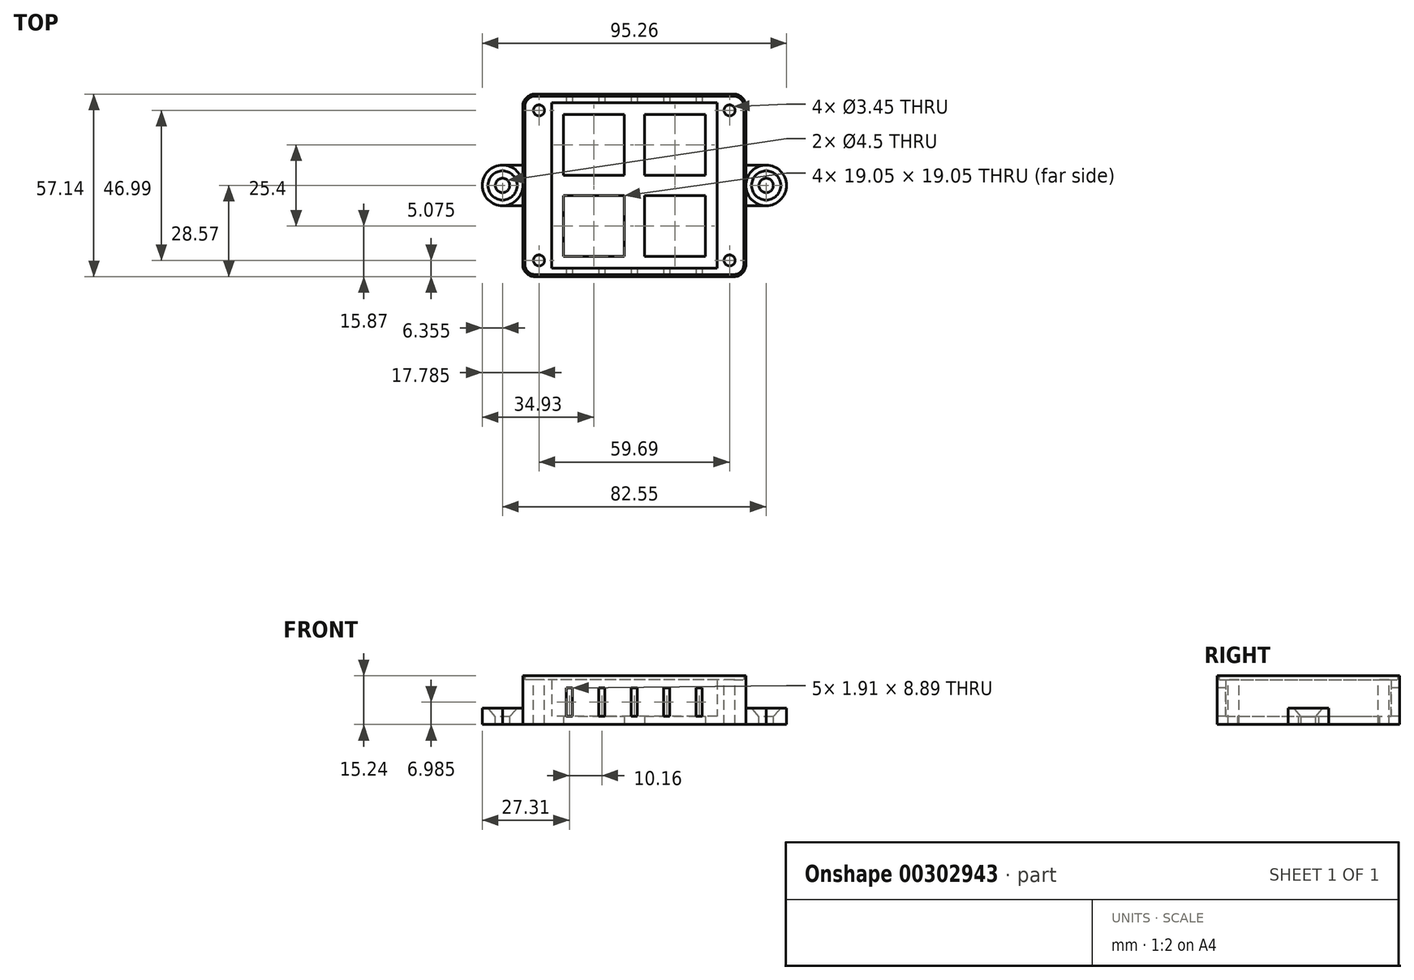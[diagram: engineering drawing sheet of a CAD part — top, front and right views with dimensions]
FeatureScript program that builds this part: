
annotation { "Feature Type Name" : "Feature", "Feature Type Description" : "" }
export const myFeature = defineFeature(function(context is Context, id is Id, definition is map)
    precondition{}
    {
        {
            var Q0;
            Q0=qCreatedBy(makeId("Top.planeOp"),FACE);
            var sketch = newSketch(context, id + "F0", { "sketchPlane" : qUnion([Q0])});
            skLineSegment(sketch, "E0.bottom", {"start": v(34.93, -28.58) * mm, "end": v(-34.92, -28.57) * mm});
            skLineSegment(sketch, "E0.top", {"start": v(34.93, 28.58) * mm, "end": v(-34.92, 28.58) * mm});
            skLineSegment(sketch, "E0.left", {"start": v(34.92, -28.58) * mm, "end": v(34.93, 28.58) * mm});
            skLineSegment(sketch, "E0.right", {"start": v(-34.93, -28.58) * mm, "end": v(-34.92, 28.58) * mm});
            skPoint(sketch, "E0.middle", {"position": v(0, 0) * mm});
            skLineSegment(sketch, "E1.bottom", {"start": v(25.9, -25.9) * mm, "end": v(-25.9, -25.9) * mm});
            skLineSegment(sketch, "E1.top", {"start": v(25.9, 25.9) * mm, "end": v(-25.9, 25.9) * mm});
            skLineSegment(sketch, "E1.left", {"start": v(25.9, -25.9) * mm, "end": v(25.9, 25.9) * mm});
            skLineSegment(sketch, "E1.right", {"start": v(-25.9, -25.9) * mm, "end": v(-25.9, 25.9) * mm});
            skCircle(sketch, "E2", {"center": v(-41.28, 0) * mm, "radius": 6.35 * mm});
            skPoint(sketch, "E2.centerSnap0", {"position": v(-25.9, 0) * mm});
            skCircle(sketch, "E3", {"center": v(41.28, 0) * mm, "radius": 6.35 * mm});
            skPoint(sketch, "E3.centerSnap0", {"position": v(34.93, 0) * mm});
            skLineSegment(sketch, "E4", {"start": v(-41.28, 6.35) * mm, "end": v(-34.92, 6.35) * mm});
            skLineSegment(sketch, "E5", {"start": v(-41.28, -6.35) * mm, "end": v(-34.92, -6.35) * mm});
            skLineSegment(sketch, "E6", {"start": v(41.28, -6.35) * mm, "end": v(34.93, -6.35) * mm});
            skLineSegment(sketch, "E7", {"start": v(41.28, 6.35) * mm, "end": v(34.93, 6.35) * mm});
            skLineSegment(sketch, "E8.bottom", {"start": v(3.17, 3.18) * mm, "end": v(22.23, 3.18) * mm});
            skLineSegment(sketch, "E8.top", {"start": v(3.17, 22.23) * mm, "end": v(22.23, 22.23) * mm});
            skLineSegment(sketch, "E8.left", {"start": v(3.17, 3.18) * mm, "end": v(3.17, 22.23) * mm});
            skLineSegment(sketch, "E8.right", {"start": v(22.23, 3.18) * mm, "end": v(22.23, 22.23) * mm});
            skPoint(sketch, "E8.middle", {"position": v(12.7, 12.7) * mm});
            skLineSegment(sketch, "E9.0.1.0", {"start": v(3.17, -22.23) * mm, "end": v(22.23, -22.23) * mm});
            skLineSegment(sketch, "E9.0.1.1", {"start": v(3.17, -22.23) * mm, "end": v(3.17, -3.18) * mm});
            skLineSegment(sketch, "E9.0.1.2", {"start": v(3.17, -3.18) * mm, "end": v(22.23, -3.18) * mm});
            skLineSegment(sketch, "E9.0.1.3", {"start": v(22.23, -22.23) * mm, "end": v(22.23, -3.18) * mm});
            skLineSegment(sketch, "E9.1.0.0", {"start": v(-22.23, 3.18) * mm, "end": v(-3.18, 3.18) * mm});
            skLineSegment(sketch, "E9.1.0.1", {"start": v(-22.23, 3.18) * mm, "end": v(-22.23, 22.23) * mm});
            skLineSegment(sketch, "E9.1.0.2", {"start": v(-22.23, 22.23) * mm, "end": v(-3.18, 22.23) * mm});
            skLineSegment(sketch, "E9.1.0.3", {"start": v(-3.17, 3.17) * mm, "end": v(-3.18, 22.23) * mm});
            skLineSegment(sketch, "E9.1.1.0", {"start": v(-22.23, -22.23) * mm, "end": v(-3.17, -22.23) * mm});
            skLineSegment(sketch, "E9.1.1.1", {"start": v(-22.23, -22.23) * mm, "end": v(-22.23, -3.18) * mm});
            skLineSegment(sketch, "E9.1.1.2", {"start": v(-22.23, -3.18) * mm, "end": v(-3.17, -3.18) * mm});
            skLineSegment(sketch, "E9.1.1.3", {"start": v(-3.17, -22.23) * mm, "end": v(-3.18, -3.18) * mm});
            skLineSegment(sketch, "E9.direction1", {"start": v(3.17, 3.18) * mm, "end": v(-22.23, 3.18) * mm, "construction": true});
            skLineSegment(sketch, "E9.direction2", {"start": v(3.17, 3.18) * mm, "end": v(3.17, -22.23) * mm, "construction": true});
            skSolve(sketch);
        }
        {
            var Q0;
            {var subQ5=sQuery(id+"F0.wireOp",EDGE,"E0.bottom");Q0=makeQuery(id+"F0.imprint","IMPRINT",FACE,{"disambiguationData":[TD([[makeQuery(id+"F0.imprint","IMPRINT",EDGE,{"derivedFrom":subQ5}),-1.0]])]});}
            extrude(context, id + "F1", {"entities" : qUnion([Q0]), "depth" : 13.97 * mm});
        }
        {
            var Q0;
            Q0=makeQuery(id+"F0.imprint","IMPRINT",FACE,{"disambiguationData":[TD([[makeQuery(id+"F0.imprint","IMPRINT",EDGE,{"derivedFrom":sQuery(id+"F0.wireOp",EDGE,"14b3595c-3327-4aa5-80dc-2c4d7012dacc")}),-1.0]])]});
            var Q1;
            {var subQ0=sQuery(id+"F0.wireOp",EDGE,"E4");Q1=makeQuery(id+"F0.imprint","IMPRINT",FACE,{"disambiguationData":[TD([[makeQuery(id+"F0.imprint","IMPRINT",EDGE,{"derivedFrom":subQ0}),-1.0]])]});}
            var Q2;
            {var subQ0=sQuery(id+"F0.wireOp",EDGE,"E7");Q2=makeQuery(id+"F0.imprint","IMPRINT",FACE,{"disambiguationData":[TD([[makeQuery(id+"F0.imprint","IMPRINT",EDGE,{"derivedFrom":subQ0}),1.0]])]});}
            var Q3;
            {var subQ0=sQuery(id+"F0.wireOp",EDGE,"E6");Q3=makeQuery(id+"F0.imprint","IMPRINT",FACE,{"disambiguationData":[TD([[makeQuery(id+"F0.imprint","IMPRINT",EDGE,{"derivedFrom":subQ0}),-1.0]])]});}
            var Q4;
            {var subQ0=sQuery(id+"F0.wireOp",EDGE,"E5");Q4=makeQuery(id+"F0.imprint","IMPRINT",FACE,{"disambiguationData":[TD([[makeQuery(id+"F0.imprint","IMPRINT",EDGE,{"derivedFrom":subQ0}),1.0]])]});}
            var Q5;
            Q5=makeQuery(id+"F0.imprint","IMPRINT",FACE,{"disambiguationData":[TD([[makeQuery(id+"F0.imprint","IMPRINT",EDGE,{"derivedFrom":sQuery(id+"F0.wireOp",EDGE,"6906daeb-3f2b-41cf-9315-c194a6f3f70c")}),-1.0]])]});
            extrude(context, id + "F2", {"entities" : qUnion([Q0, Q1, Q2, Q3, Q4, Q5]), "operationType" : NewBodyOperationType.ADD, "depth" : 5.08 * mm});
        }
        {
            var Q0;
            Q0=makeQuery(id+"F0.imprint","IMPRINT",FACE,{"disambiguationData":[TD([[makeQuery(id+"F0.imprint","IMPRINT",EDGE,{"derivedFrom":sQuery(id+"F0.wireOp",EDGE,"E1.bottom")}),-1.0]])]});
            extrude(context, id + "F3", {"entities" : qUnion([Q0]), "operationType" : NewBodyOperationType.ADD, "depth" : 2.54 * mm});
        }
        {
            var Q0;
            Q0=makeQuery(id+"F1.opExtrude","SWEPT_EDGE",EDGE,{"disambiguationData":[OSD([sQuery(id+"F0.wireOp",EDGE,"E0.bottom"),sQuery(id+"F0.wireOp",EDGE,"E0.right")])]});
            var Q1;
            Q1=makeQuery(id+"F1.opExtrude","SWEPT_EDGE",EDGE,{"disambiguationData":[OSD([sQuery(id+"F0.wireOp",EDGE,"E0.top"),sQuery(id+"F0.wireOp",EDGE,"E0.left")])]});
            var Q2;
            Q2=makeQuery(id+"F1.opExtrude","SWEPT_EDGE",EDGE,{"disambiguationData":[OSD([sQuery(id+"F0.wireOp",EDGE,"E0.bottom"),sQuery(id+"F0.wireOp",EDGE,"E0.left")])]});
            var Q3;
            Q3=makeQuery(id+"F1.opExtrude","SWEPT_EDGE",EDGE,{"disambiguationData":[OSD([sQuery(id+"F0.wireOp",EDGE,"E0.top"),sQuery(id+"F0.wireOp",EDGE,"E0.right")])]});
            fillet(context, id + "F4", {"entities" : qUnion([Q0, Q1, Q2, Q3]), "radius" : 3.8 * mm, "tangentPropagation" : true, "allowEdgeOverflow" : false});
        }
        {
            var Q0;
            Q0=qCreatedBy(makeId("Top.planeOp"),FACE);
            cPlane(context, id + "F5", {"entities" : qUnion([Q0]), "cplaneType" : CPlaneType.OFFSET, "offset" : 13.97 * mm, "width" : 152.4 * mm, "height" : 152.4 * mm});
        }
        {
            var Q0;
            Q0=qCreatedBy(id+"F5.planeOp",FACE);
            var sketch = newSketch(context, id + "F6", { "sketchPlane" : qUnion([Q0])});
            skPoint(sketch, "E10", {"position": v(-29.85, -23.5) * mm});
            skPoint(sketch, "E11", {"position": v(-29.84, 23.5) * mm});
            skPoint(sketch, "E12", {"position": v(29.84, -23.5) * mm});
            skPoint(sketch, "E13", {"position": v(29.85, 23.5) * mm});
            skSolve(sketch);
        }
        {
            var Q0;
            Q0=sQuery(id+"F6.wireOp",VERTEX,"E11");
            var Q1;
            Q1=sQuery(id+"F6.wireOp",VERTEX,"E10");
            var Q2;
            Q2=sQuery(id+"F6.wireOp",VERTEX,"E12");
            var Q3;
            Q3=sQuery(id+"F6.wireOp",VERTEX,"E13");
            var Q4;
            Q4=makeQuery(id+"F1.opExtrude","SWEPT_BODY",BODY,{"disambiguationData":[OSD([sQuery(id+"F0.wireOp",EDGE,"E0.bottom"),sQuery(id+"F0.wireOp",EDGE,"E0.top"),sQuery(id+"F0.wireOp",EDGE,"E0.left"),sQuery(id+"F0.wireOp",EDGE,"E0.right"),sQuery(id+"F0.wireOp",EDGE,"E1.bottom"),sQuery(id+"F0.wireOp",EDGE,"E1.top"),sQuery(id+"F0.wireOp",EDGE,"E1.left"),sQuery(id+"F0.wireOp",EDGE,"E1.right")])]});
            hole(context, id + "F7", {"style" : HoleStyle.SIMPLE, "endStyle" : HoleEndStyle.THROUGH, "standardTappedOrClearance" : lookupTablePath({ "standard" : "ANSI", "fit" : "Normal (ASME)", "engagement" : "75%", "pitch" : "32 tpi", "size" : "#8", "type" : "Tapped" }), "standardBlindInLast" : lookupTablePath({ "fit" : "Free", "standard" : "ANSI", "engagement" : "75%", "pitch" : "32 tpi", "size" : "#8", "type" : "Tapped" }), "holeDiameter" : 3.45 * mm, "showTappedDepth" : true, "tappedDepth" : 13.97 * mm, "tapClearance" : 3, "locations" : qUnion([Q0, Q1, Q2, Q3]), "scope" : qUnion([Q4]), "majorDiameter" : 4.17 * mm});
        }
        {
            var Q0;
            Q0=qCreatedBy(makeId("Front.planeOp"),FACE);
            cPlane(context, id + "F8", {"entities" : qUnion([Q0]), "cplaneType" : CPlaneType.OFFSET, "offset" : 28.57 * mm, "width" : 152.4 * mm, "height" : 152.4 * mm});
        }
        {
            var Q0;
            Q0=qCreatedBy(id+"F8.planeOp",FACE);
            var sketch = newSketch(context, id + "F9", { "sketchPlane" : qUnion([Q0])});
            skPoint(sketch, "E14", {"position": v(0, 6.99) * mm});
            skLineSegment(sketch, "E15.bottom", {"start": v(0.95, 2.54) * mm, "end": v(-0.95, 2.54) * mm});
            skLineSegment(sketch, "E15.top", {"start": v(0.95, 11.43) * mm, "end": v(-0.95, 11.43) * mm});
            skLineSegment(sketch, "E15.left", {"start": v(0.95, 2.54) * mm, "end": v(0.95, 11.43) * mm});
            skLineSegment(sketch, "E15.right", {"start": v(-0.95, 2.54) * mm, "end": v(-0.95, 11.43) * mm});
            skLineSegment(sketch, "E16.1.0.0", {"start": v(11.11, 11.43) * mm, "end": v(9.2, 11.43) * mm});
            skLineSegment(sketch, "E16.1.0.1", {"start": v(11.11, 2.54) * mm, "end": v(11.11, 11.43) * mm});
            skLineSegment(sketch, "E16.1.0.2", {"start": v(9.2, 2.54) * mm, "end": v(9.2, 11.43) * mm});
            skLineSegment(sketch, "E16.1.0.3", {"start": v(11.11, 2.54) * mm, "end": v(9.2, 2.54) * mm});
            skLineSegment(sketch, "E16.2.0.0", {"start": v(21.27, 11.43) * mm, "end": v(19.37, 11.43) * mm});
            skLineSegment(sketch, "E16.2.0.1", {"start": v(21.27, 2.54) * mm, "end": v(21.27, 11.43) * mm});
            skLineSegment(sketch, "E16.2.0.2", {"start": v(19.37, 2.54) * mm, "end": v(19.37, 11.43) * mm});
            skLineSegment(sketch, "E16.2.0.3", {"start": v(21.27, 2.54) * mm, "end": v(19.37, 2.54) * mm});
            skLineSegment(sketch, "E17.1.0.0", {"start": v(-9.2, 11.43) * mm, "end": v(-11.11, 11.43) * mm});
            skLineSegment(sketch, "E17.1.0.1", {"start": v(-9.2, 2.54) * mm, "end": v(-9.2, 11.43) * mm});
            skLineSegment(sketch, "E17.1.0.2", {"start": v(-11.11, 2.54) * mm, "end": v(-11.11, 11.43) * mm});
            skLineSegment(sketch, "E17.1.0.3", {"start": v(-9.2, 2.54) * mm, "end": v(-11.11, 2.54) * mm});
            skLineSegment(sketch, "E17.2.0.0", {"start": v(-19.37, 11.43) * mm, "end": v(-21.27, 11.43) * mm});
            skLineSegment(sketch, "E17.2.0.1", {"start": v(-19.37, 2.54) * mm, "end": v(-19.37, 11.43) * mm});
            skLineSegment(sketch, "E17.2.0.2", {"start": v(-21.27, 2.54) * mm, "end": v(-21.27, 11.43) * mm});
            skLineSegment(sketch, "E17.2.0.3", {"start": v(-19.37, 2.54) * mm, "end": v(-21.27, 2.54) * mm});
            skLineSegment(sketch, "E17.direction1", {"start": v(-0.95, 2.54) * mm, "end": v(-11.11, 2.54) * mm, "construction": true});
            skSolve(sketch);
        }
        {
            var Q0;
            Q0=makeQuery(id+"F9.imprint","IMPRINT",FACE,{"disambiguationData":[TD([[makeQuery(id+"F9.imprint","IMPRINT",EDGE,{"derivedFrom":sQuery(id+"F9.wireOp",EDGE,"E16.1.0.0")}),1.0]])]});
            var Q1;
            Q1=makeQuery(id+"F9.imprint","IMPRINT",FACE,{"disambiguationData":[TD([[makeQuery(id+"F9.imprint","IMPRINT",EDGE,{"derivedFrom":sQuery(id+"F9.wireOp",EDGE,"E15.bottom")}),-1.0]])]});
            var Q2;
            Q2=makeQuery(id+"F9.imprint","IMPRINT",FACE,{"disambiguationData":[TD([[makeQuery(id+"F9.imprint","IMPRINT",EDGE,{"derivedFrom":sQuery(id+"F9.wireOp",EDGE,"E17.2.0.0")}),1.0]])]});
            var Q3;
            Q3=makeQuery(id+"F9.imprint","IMPRINT",FACE,{"disambiguationData":[TD([[makeQuery(id+"F9.imprint","IMPRINT",EDGE,{"derivedFrom":sQuery(id+"F9.wireOp",EDGE,"E17.1.0.0")}),1.0]])]});
            var Q4;
            Q4=makeQuery(id+"F9.imprint","IMPRINT",FACE,{"disambiguationData":[TD([[makeQuery(id+"F9.imprint","IMPRINT",EDGE,{"derivedFrom":sQuery(id+"F9.wireOp",EDGE,"E16.2.0.0")}),1.0]])]});
            extrude(context, id + "F10", {"entities" : qUnion([Q0, Q1, Q2, Q3, Q4]), "operationType" : NewBodyOperationType.REMOVE, "oppositeDirection" : true, "depth" : 57.15 * mm});
        }
        {
            var Q0;
            {var subQ0=sQuery(id+"F0.wireOp",EDGE,"E3");var subQ1=makeQuery(id+"F0.imprint","INTERSECT",VERTEX,{"derivedFrom":[subQ0,sQuery(id+"F0.wireOp",EDGE,"E7")]});Q0=makeQuery(id+"F0.imprint","IMPRINT",FACE,{"disambiguationData":[TD([[makeQuery(id+"F0.imprint","IMPRINT",EDGE,{"disambiguationData":[TD([[subQ1,-1.0]])],"derivedFrom":subQ0}),1.0]])]});}
            var Q1;
            {var subQ0=sQuery(id+"F0.wireOp",EDGE,"E2");var subQ1=makeQuery(id+"F0.imprint","INTERSECT",VERTEX,{"derivedFrom":[subQ0,sQuery(id+"F0.wireOp",EDGE,"E4")]});Q1=makeQuery(id+"F0.imprint","IMPRINT",FACE,{"disambiguationData":[TD([[makeQuery(id+"F0.imprint","IMPRINT",EDGE,{"disambiguationData":[TD([[subQ1,1.0]])],"derivedFrom":subQ0}),1.0]])]});}
            extrude(context, id + "F11", {"entities" : qUnion([Q0, Q1]), "depth" : 5.08 * mm});
        }
        {
            var Q0;
            Q0=qCreatedBy(makeId("Top.planeOp"),FACE);
            cPlane(context, id + "F12", {"entities" : qUnion([Q0]), "cplaneType" : CPlaneType.OFFSET, "offset" : 5.08 * mm, "width" : 152.4 * mm, "height" : 152.4 * mm});
        }
        {
            var Q0;
            Q0=qCreatedBy(id+"F12.planeOp",FACE);
            var sketch = newSketch(context, id + "F13", { "sketchPlane" : qUnion([Q0])});
            skPoint(sketch, "E18", {"position": v(-41.28, 0) * mm});
            skPoint(sketch, "E19", {"position": v(41.28, 0) * mm});
            skSolve(sketch);
        }
        {
            var Q0;
            Q0=sQuery(id+"F13.wireOp",VERTEX,"E18");
            var Q1;
            Q1=sQuery(id+"F13.wireOp",VERTEX,"E19");
            var Q2;
            Q2=makeQuery(id+"F11.opExtrude","SWEPT_BODY",BODY,{"disambiguationData":[OSD([sQuery(id+"F0.wireOp",EDGE,"E2")])]});
            var Q3;
            Q3=makeQuery(id+"F11.opExtrude","SWEPT_BODY",BODY,{"disambiguationData":[OSD([sQuery(id+"F0.wireOp",EDGE,"E3")])]});
            hole(context, id + "F14", {"style" : HoleStyle.C_SINK, "endStyle" : HoleEndStyle.THROUGH, "standardTappedOrClearance" : lookupTablePath({ "standard" : "ANSI", "fit" : "Normal (ASME)", "size" : "#8", "type" : "Clearance" }), "standardBlindInLast" : lookupTablePath({ "fit" : "Free", "standard" : "ANSI", "size" : "#8", "type" : "Clearance" }), "holeDiameter" : 4.5 * mm, "cSinkDiameter" : 9.12 * mm, "cSinkAngle" : 82 * degree, "tappedDepth" : 12.7 * mm, "tapClearance" : 3, "locations" : qUnion([Q0, Q1]), "scope" : qUnion([Q2, Q3])});
        }
        {
            var Q0;
            Q0=makeQuery(id+"F1.opExtrude","CAP_FACE",FACE,{"disambiguationData":[OSD([sQuery(id+"F0.wireOp",EDGE,"E0.bottom"),sQuery(id+"F0.wireOp",EDGE,"E0.top"),sQuery(id+"F0.wireOp",EDGE,"E0.left"),sQuery(id+"F0.wireOp",EDGE,"E0.right"),sQuery(id+"F0.wireOp",EDGE,"E1.bottom"),sQuery(id+"F0.wireOp",EDGE,"E1.top"),sQuery(id+"F0.wireOp",EDGE,"E1.left"),sQuery(id+"F0.wireOp",EDGE,"E1.right")])],"isStart":false});
            var sketch = newSketch(context, id + "F15", { "sketchPlane" : qUnion([Q0])});
            skLineSegment(sketch, "E20.0", {"start": v(34.29, -24.77) * mm, "end": v(34.3, 24.77) * mm});
            skArc(sketch, "E20.1", {"start": v(31.11, -27.94) * mm, "mid": v(33.36, -27.01) * mm, "end": v(34.29, -24.77) * mm});
            skArc(sketch, "E20.2", {"start": v(34.3, 24.77) * mm, "mid": v(33.36, 27.01) * mm, "end": v(31.12, 27.94) * mm});
            skLineSegment(sketch, "E20.3", {"start": v(31.11, -27.94) * mm, "end": v(-31.11, -27.94) * mm});
            skLineSegment(sketch, "E20.4", {"start": v(31.12, 27.94) * mm, "end": v(-31.11, 27.94) * mm});
            skArc(sketch, "E20.5", {"start": v(-31.11, 27.94) * mm, "mid": v(-33.36, 27.01) * mm, "end": v(-34.29, 24.77) * mm});
            skLineSegment(sketch, "E20.6", {"start": v(-34.3, -24.77) * mm, "end": v(-34.29, 24.77) * mm});
            skArc(sketch, "E20.7", {"start": v(-34.29, -24.77) * mm, "mid": v(-33.36, -27.01) * mm, "end": v(-31.11, -27.94) * mm});
            skSolve(sketch);
        }
        {
            var Q0;
            Q0=makeQuery(id+"F15.imprint","IMPRINT",FACE,{"disambiguationData":[TD([[makeQuery(id+"F15.imprint","IMPRINT",EDGE,{"derivedFrom":sQuery(id+"F15.wireOp",EDGE,"E20.0")}),-1.0]])]});
            extrude(context, id + "F16", {"entities" : qUnion([Q0]), "operationType" : NewBodyOperationType.ADD, "depth" : 1.27 * mm});
        }
    });
